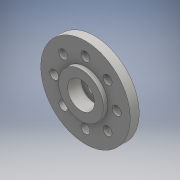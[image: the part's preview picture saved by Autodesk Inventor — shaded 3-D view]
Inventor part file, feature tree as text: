
AUTODESK INVENTOR PART (.ipt)
format: ipt  version: 2016 (Build 200138000, 138)  size: 152,576 bytes
history: native  units: mm
features: extrude x6, sketch x6, other x1
ambient origin geometry x8: Origin, YZ Plane, XZ Plane, XY Plane, X Axis, Y Axis, Z Axis, Center Point
bodies: Body1 (feature_tree)
feature tree (13):
  other  "ソリッド1"
  extrude  "押し出し1"  Depth=20.0mm
  extrude  "押し出し2"  Depth=2.0mm TaperAngle=0.0deg
  extrude  "押し出し3"  Depth=14.0mm
  extrude  "押し出し4"  Depth=2.0mm
  extrude  "押し出し5"  Depth=2.0mm
  extrude  "押し出し6"  Depth=2.0mm
  sketch  "スケッチ1"
  sketch  "スケッチ2"
  sketch  "スケッチ3"
  sketch  "スケッチ4"
  sketch  "スケッチ5"
  sketch  "スケッチ6"
